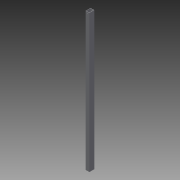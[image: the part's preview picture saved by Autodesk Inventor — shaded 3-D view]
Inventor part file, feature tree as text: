
AUTODESK INVENTOR PART (.ipt)
format: ipt  version: 2013 (Build 170138000, 138)  size: 85,504 bytes
history: native  units: in
note: dims shown in document units (in); Inventor stores cm internally (conversion verified against a paired STEP export)
features: other x4, hole x1, sketch x1
ambient origin geometry x8: Origin, YZ Plane, XZ Plane, XY Plane, X Axis, Y Axis, Z Axis, Center Point
bodies: Solid1 (feature_tree)
feature tree (6):
  other  "Table"
  other  "squareTube1.5x2.ipt"
  hole  "Hole1"  [1 undecoded]
  other  "Solid1::squareTube1.5x2.ipt"
  other  "TaggingFeature1"
  sketch  "Sketch1"  dims[d0=1.5in d1=2.0in d2=0.125in d4=0.0in d3=1.5in d5=0.75in d6=0.5in d7=0.25in d8=0.75in d9=0.375in d10=0.25in d11=0.5635in d12=1.0in d13=0.8108in]
note: 1 required parameter value undecoded (feature->parameter linkage not recoverable at this tier; creation-order binding heuristic only, values carry confidence <= 0.55)
